# Revit family: Shower-Shower_Column_Kit-KOHLER-JULY-K-23126T
name_source: partatom
category: Plumbing Fixtures
units: mm (PartAtom-declared; Revit-internal decimal feet)

## family parameters
Cut with Voids When Loaded = No
Host = Face
OmniClass Number = 23.31.17.00
OmniClass Title = Showers
Part Type = Normal
Room Calculation Point = No
Round Connector Dimension = Use Diameter
Shared = No

## types (3) — shared parameters
ADA Compliant = No
Assembly Code = D2010700
CW Connection = Yes
Cold Water Inlet = Cold Water Inlet
Date Modified = 03/26/2024
Default Elevation = 42"
Drain Included = No
Flow Rate = 8 GPM
HW Connection = Yes
Handle Clearance = 2 3/8"
Height = 50 1/2"
Hot Water Inlet = Hot Water Inlet
Length = 23 13/16"
Manufacturer = Kohler Co.
Master Format 2014 = 22 42 23
Master Format 2014 Name = Residential Showers
Material = Premium Metal Construction
Pressure = 60.00 psi
Product Name = JULY
Spout Reach = 3 5/8"
URL = http://www.kohler.com.cn
Vent Connection = No
Waste Connection = No
Waste Water Outlet = Waste Water Outlet
WaterSense Certified = No
Width = 11 1/8"

## per-type parameters (varying)
| type | 9 | B9 | Description | Finish | Model | Product Documentation Link | Product Page URL | Type |
| 9, CP-Polished Chrome | Yes | No | three-outlet shower column hard pipe link (comfortable version) | Kohler-Metal-CP-Polished_Chrome | K-23126T-9-CP | https://files.kohler.com.cn | https://www.kohler.com.cn | 1 |
| B9, 2BL-Black | No | Yes | three water shower column hard pipe link | KOHLER-Metal-2BL-Black | K-23126T-B9-2BL | https://files.kohler.com.cn | https://www.kohler.com.cn | 2 |
| B9, BL-Matte Black | No | Yes | three water shower column hard pipe link | Kohler-Metal-BL-Matte_Black | K-23126T-B9-BL | https://www.kohler.com.cn |  | 3 |

## geometry (parser evidence)
native form markers: Sweep x7
no freeform markers — native parametric forms only
